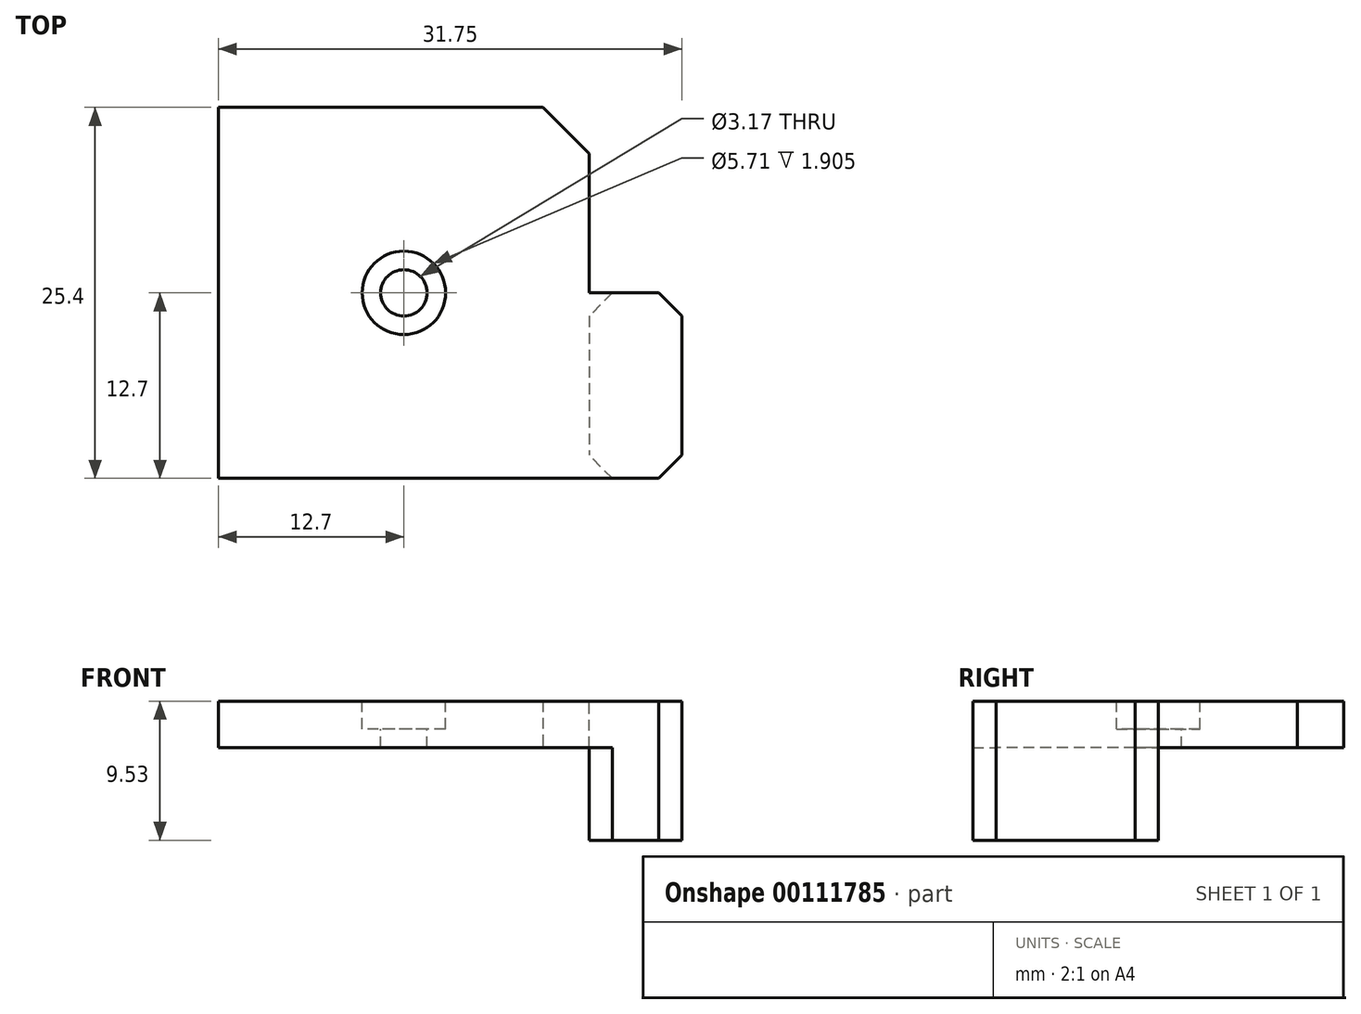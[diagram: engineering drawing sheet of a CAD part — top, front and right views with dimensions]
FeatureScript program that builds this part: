
annotation { "Feature Type Name" : "Feature", "Feature Type Description" : "" }
export const myFeature = defineFeature(function(context is Context, id is Id, definition is map)
    precondition{}
    {
        {
            var Q0;
            Q0=qCreatedBy(makeId("Top.planeOp"),FACE);
            var sketch = newSketch(context, id + "F0", { "sketchPlane" : qUnion([Q0])});
            skLineSegment(sketch, "E0.bottom", {"start": v(12.7, 12.7) * mm, "end": v(-12.7, 12.7) * mm});
            skLineSegment(sketch, "E0.top", {"start": v(12.7, -12.7) * mm, "end": v(-12.7, -12.7) * mm});
            skLineSegment(sketch, "E0.left", {"start": v(12.7, 12.7) * mm, "end": v(12.7, -12.7) * mm});
            skLineSegment(sketch, "E0.right", {"start": v(-12.7, 12.7) * mm, "end": v(-12.7, -12.7) * mm});
            skPoint(sketch, "E0.middle", {"position": v(0, 0) * mm});
            skLineSegment(sketch, "E1", {"start": v(12.7, 0) * mm, "end": v(12.7, -12.7) * mm});
            skLineSegment(sketch, "E2", {"start": v(12.7, -12.7) * mm, "end": v(19.05, -12.7) * mm});
            skLineSegment(sketch, "E3.bottom", {"start": v(12.7, 0) * mm, "end": v(19.05, 0) * mm});
            skLineSegment(sketch, "E3.right", {"start": v(19.05, 0) * mm, "end": v(19.05, -12.7) * mm});
            skSolve(sketch);
        }
        {
            var Q0;
            Q0=makeQuery(id+"F0.imprint","IMPRINT",FACE,{"disambiguationData":[TD([[makeQuery(id+"F0.imprint","IMPRINT",EDGE,{"derivedFrom":sQuery(id+"F0.wireOp",EDGE,"E3.bottom")}),-1.0]])]});
            var Q1;
            Q1=makeQuery(id+"F0.imprint","IMPRINT",FACE,{"disambiguationData":[TD([[makeQuery(id+"F0.imprint","IMPRINT",EDGE,{"derivedFrom":sQuery(id+"F0.wireOp",EDGE,"E0.bottom")}),1.0]])]});
            extrude(context, id + "F1", {"entities" : qUnion([Q0, Q1]), "oppositeDirection" : true, "depth" : 3.17 * mm});
        }
        {
            var Q0;
            Q0=makeQuery(id+"F1.opExtrude","CAP_FACE",FACE,{"disambiguationData":[OSD([sQuery(id+"F0.wireOp",EDGE,"E0.bottom"),sQuery(id+"F0.wireOp",EDGE,"E0.top"),sQuery(id+"F0.wireOp",EDGE,"E0.left"),sQuery(id+"F0.wireOp",EDGE,"E0.right"),sQuery(id+"F0.wireOp",EDGE,"E3.bottom"),sQuery(id+"F0.wireOp",EDGE,"E2"),sQuery(id+"F0.wireOp",EDGE,"E3.right")])],"isStart":false});
            var sketch = newSketch(context, id + "F2", { "sketchPlane" : qUnion([Q0])});
            skLineSegment(sketch, "E4", {"start": v(12.7, 0) * mm, "end": v(12.7, 12.7) * mm});
            skSolve(sketch);
        }
        {
            var Q0;
            Q0 = qSketchRegion(id + "F2", true);
            var Q1;
            {var subQ0=sQuery(id+"F2.wireOp",EDGE,"E4");Q1=makeQuery(id+"F2.imprint","IMPRINT",FACE,{"disambiguationData":[TD([[makeQuery(id+"F2.imprint","IMPRINT",EDGE,{"derivedFrom":subQ0}),-1.0]])]});}
            extrude(context, id + "F3", {"entities" : qUnion([Q0, Q1]), "operationType" : NewBodyOperationType.ADD, "depth" : 6.35 * mm});
        }
        {
            var Q0;
            Q0=makeQuery(id+"F1.opExtrude","CAP_FACE",FACE,{"disambiguationData":[OSD([sQuery(id+"F0.wireOp",EDGE,"E0.bottom"),sQuery(id+"F0.wireOp",EDGE,"E0.top"),sQuery(id+"F0.wireOp",EDGE,"E0.left"),sQuery(id+"F0.wireOp",EDGE,"E0.right"),sQuery(id+"F0.wireOp",EDGE,"E3.bottom"),sQuery(id+"F0.wireOp",EDGE,"E2"),sQuery(id+"F0.wireOp",EDGE,"E3.right")])],"isStart":true});
            var sketch = newSketch(context, id + "F4", { "sketchPlane" : qUnion([Q0])});
            skPoint(sketch, "E5", {"position": v(0, 0) * mm});
            skSolve(sketch);
        }
        {
            var Q0;
            Q0=sQuery(id+"F4.wireOp",VERTEX,"E5");
            var Q1;
            Q1=makeQuery(id+"F1.opExtrude","SWEPT_BODY",BODY,{"disambiguationData":[OSD([sQuery(id+"F0.wireOp",EDGE,"E0.bottom"),sQuery(id+"F0.wireOp",EDGE,"E0.top"),sQuery(id+"F0.wireOp",EDGE,"E0.left"),sQuery(id+"F0.wireOp",EDGE,"E0.right"),sQuery(id+"F0.wireOp",EDGE,"E3.bottom"),sQuery(id+"F0.wireOp",EDGE,"E2"),sQuery(id+"F0.wireOp",EDGE,"E3.right")])]});
            hole(context, id + "F5", {"style" : HoleStyle.C_BORE, "endStyle" : HoleEndStyle.THROUGH, "holeDiameter" : 3.17 * mm, "cBoreDiameter" : 5.7 * mm, "cBoreDepth" : 1.9 * mm, "startFromSketch" : true, "locations" : qUnion([Q0]), "scope" : qUnion([Q1]), "isTappedThrough" : true});
        }
        {
            var Q0;
            Q0=makeQuery(id+"F1.opExtrude","SWEPT_EDGE",EDGE,{"disambiguationData":[OSD([sQuery(id+"F0.wireOp",EDGE,"E0.bottom"),sQuery(id+"F0.wireOp",EDGE,"E0.left")])]});
            chamfer(context, id + "F6", {"entities" : qUnion([Q0]), "width" : 3.17 * mm, "tangentPropagation" : true});
        }
        {
            var Q0;
            {var subQ0=sQuery(id+"F0.wireOp",EDGE,"E3.right");var subQ1=sQuery(id+"F0.wireOp",EDGE,"E3.bottom");Q0=makeQuery(id+"F3.boolean.opBoolean","MERGE",EDGE,{"derivedFrom":[makeQuery(id+"F1.opExtrude","SWEPT_EDGE",EDGE,{"disambiguationData":[OSD([subQ1,subQ0])]}),makeQuery(id+"F3.opExtrude","SWEPT_EDGE",EDGE,{"disambiguationData":[OSD([subQ1,subQ0])]})]});}
            chamfer(context, id + "F7", {"entities" : qUnion([Q0]), "width" : 1.59 * mm, "tangentPropagation" : true});
        }
        {
            var Q0;
            {var subQ0=sQuery(id+"F0.wireOp",EDGE,"E3.right");var subQ1=sQuery(id+"F0.wireOp",EDGE,"E2");Q0=makeQuery(id+"F3.boolean.opBoolean","MERGE",EDGE,{"derivedFrom":[makeQuery(id+"F1.opExtrude","SWEPT_EDGE",EDGE,{"disambiguationData":[OSD([subQ1,subQ0])]}),makeQuery(id+"F3.opExtrude","SWEPT_EDGE",EDGE,{"disambiguationData":[OSD([sQuery(id+"F0.wireOp",EDGE,"E0.top"),subQ1,subQ0])]})]});}
            chamfer(context, id + "F8", {"entities" : qUnion([Q0]), "width" : 1.59 * mm, "tangentPropagation" : true});
        }
        {
            var Q0;
            Q0=makeQuery(id+"F3.opExtrude","SWEPT_EDGE",EDGE,{"disambiguationData":[OSD([sQuery(id+"F0.wireOp",EDGE,"E0.left"),sQuery(id+"F0.wireOp",EDGE,"E3.bottom"),sQuery(id+"F2.wireOp",EDGE,"E4")])]});
            chamfer(context, id + "F9", {"entities" : qUnion([Q0]), "width" : 1.59 * mm, "tangentPropagation" : true});
        }
        {
            var Q0;
            Q0=makeQuery(id+"F3.opExtrude","SWEPT_EDGE",EDGE,{"disambiguationData":[OSD([sQuery(id+"F0.wireOp",EDGE,"E0.top"),sQuery(id+"F0.wireOp",EDGE,"E2"),sQuery(id+"F2.wireOp",EDGE,"E4")])]});
            chamfer(context, id + "F10", {"entities" : qUnion([Q0]), "width" : 1.59 * mm, "tangentPropagation" : true});
        }
    });
